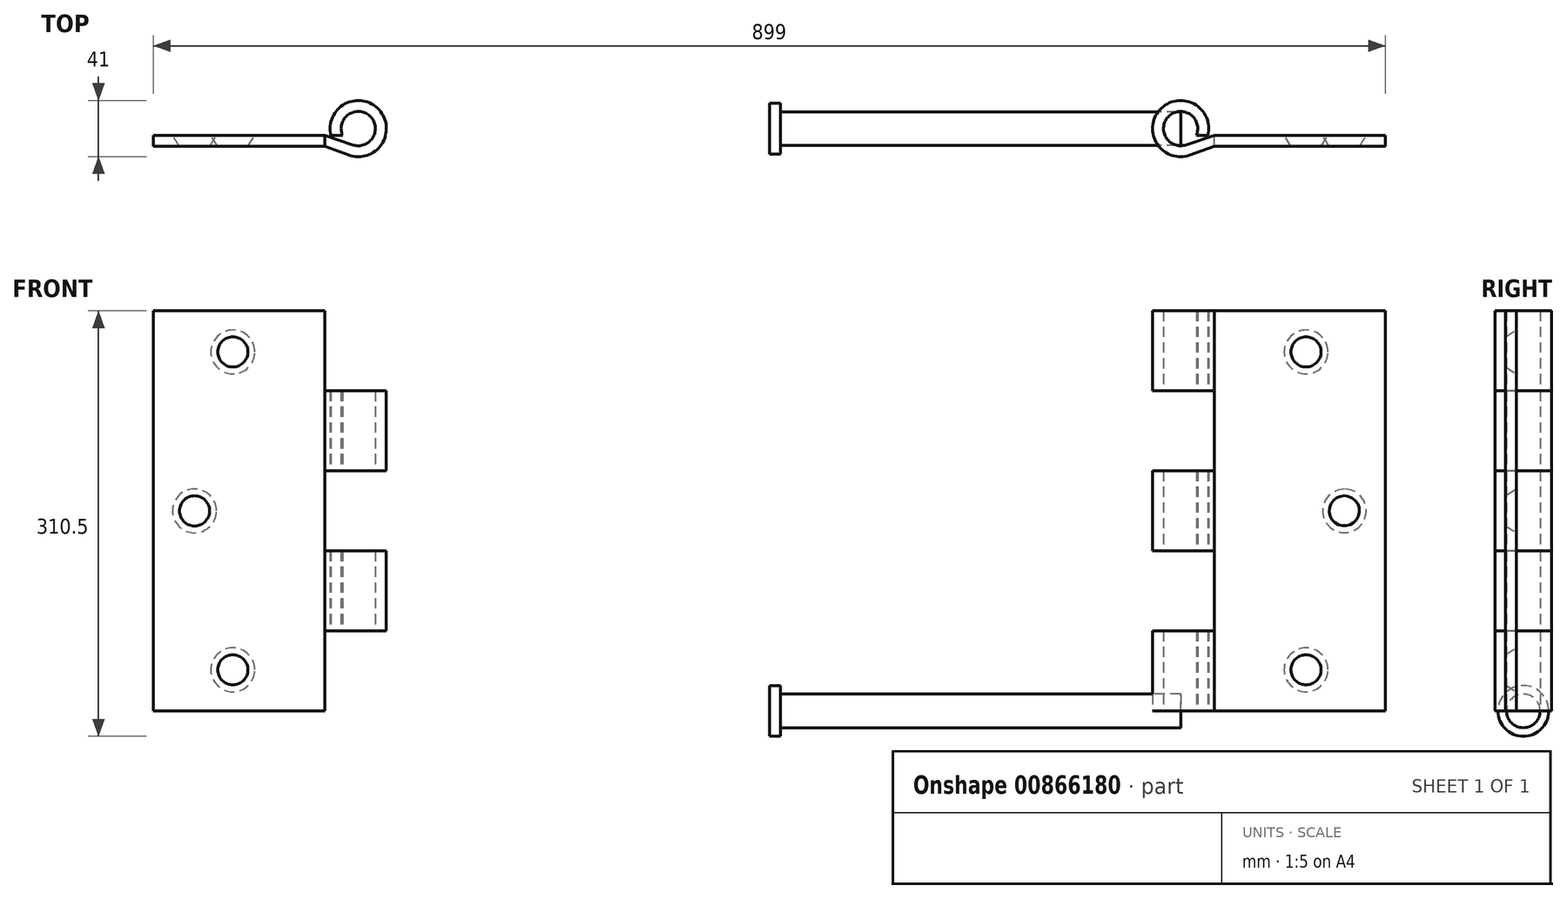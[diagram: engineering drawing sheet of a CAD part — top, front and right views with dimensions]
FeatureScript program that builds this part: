
annotation { "Feature Type Name" : "Feature", "Feature Type Description" : "" }
export const myFeature = defineFeature(function(context is Context, id is Id, definition is map)
    precondition{}
    {
        {
            var Q0;
            Q0=qCreatedBy(makeId("Top.planeOp"),FACE);
            var sketch = newSketch(context, id + "F0", { "sketchPlane" : qUnion([Q0])});
            skArc(sketch, "E0", {"start": v(-6.91, -19.3) * mm, "mid": v(15.19, 13.77) * mm, "end": v(-19.88, -5) * mm});
            skArc(sketch, "E1", {"start": v(-3.96, -11.86) * mm, "mid": v(8.44, 9.22) * mm, "end": v(-11.46, -5) * mm});
            skLineSegment(sketch, "E2", {"start": v(-149.5, -5) * mm, "end": v(-149.5, -13) * mm});
            skLineSegment(sketch, "E3", {"start": v(-149.5, -13) * mm, "end": v(-24.5, -13) * mm});
            skLineSegment(sketch, "E4", {"start": v(-24.5, -5) * mm, "end": v(-3.96, -11.86) * mm});
            skLineSegment(sketch, "E5", {"start": v(-24.5, -13) * mm, "end": v(-6.91, -19.3) * mm});
            skLineSegment(sketch, "E6.trimOffspring", {"start": v(-24.5, -5) * mm, "end": v(-149.5, -5) * mm});
            skLineSegment(sketch, "E7", {"start": v(-19.88, -5) * mm, "end": v(-11.46, -5) * mm});
            skSolve(sketch);
        }
        {
            var Q0;
            Q0=makeQuery(id+"F0.imprint","IMPRINT",FACE,{"disambiguationData":[TD([[makeQuery(id+"F0.imprint","IMPRINT",EDGE,{"derivedFrom":sQuery(id+"F0.wireOp",EDGE,"E0")}),1.0]])]});
            extrude(context, id + "F1", {"entities" : qUnion([Q0]), "depth" : 292 * mm, "offsetDistance" : 25 * mm});
        }
        {
            var Q0;
            Q0=makeQuery(id+"F1.opExtrude","SWEPT_FACE",FACE,{"disambiguationData":[OSD([sQuery(id+"F0.wireOp",EDGE,"E6.trimOffspring")])]});
            var sketch = newSketch(context, id + "F2", { "sketchPlane" : qUnion([Q0])});
            skCircle(sketch, "E8", {"center": v(119.5, 146) * mm, "radius": 16 * mm});
            skLineSegment(sketch, "E9", {"start": v(149.5, 30) * mm, "end": v(91.5, 30) * mm});
            skCircle(sketch, "E10", {"center": v(91.5, 30) * mm, "radius": 16 * mm});
            skCircle(sketch, "E11", {"center": v(91.5, 262) * mm, "radius": 16 * mm});
            skSolve(sketch);
        }
        {
            var Q0;
            Q0=makeQuery(id+"F1.opExtrude","SWEPT_FACE",FACE,{"disambiguationData":[OSD([sQuery(id+"F0.wireOp",EDGE,"E3")])]});
            var sketch = newSketch(context, id + "F3", { "sketchPlane" : qUnion([Q0])});
            skCircle(sketch, "E12", {"center": v(-91.5, 30) * mm, "radius": 11 * mm});
            skCircle(sketch, "E13", {"center": v(-119.43, 146) * mm, "radius": 11 * mm});
            skCircle(sketch, "E14", {"center": v(-91.5, 262) * mm, "radius": 11 * mm});
            skSolve(sketch);
        }
        {
            var Q1;
            Q1=makeQuery(id+"F2.imprint","IMPRINT",FACE,{"disambiguationData":[TD([[makeQuery(id+"F2.imprint","IMPRINT",EDGE,{"derivedFrom":sQuery(id+"F2.wireOp",EDGE,"E11")}),1.0]])]});
            var Q2;
            Q2=makeQuery(id+"F3.imprint","IMPRINT",FACE,{"disambiguationData":[TD([[makeQuery(id+"F3.imprint","IMPRINT",EDGE,{"derivedFrom":sQuery(id+"F3.wireOp",EDGE,"E14")}),1.0]])]});
            loft(context, id + "F4", {"operationType" : NewBodyOperationType.REMOVE, "sheetProfilesArray" : [{ "sheetProfileEntities" : qUnion([Q1]) }, { "sheetProfileEntities" : qUnion([Q2]) }]});
        }
        {
            var Q1;
            Q1=makeQuery(id+"F2.imprint","IMPRINT",FACE,{"disambiguationData":[TD([[makeQuery(id+"F2.imprint","IMPRINT",EDGE,{"derivedFrom":sQuery(id+"F2.wireOp",EDGE,"E8")}),1.0]])]});
            var Q2;
            Q2=makeQuery(id+"F3.imprint","IMPRINT",FACE,{"disambiguationData":[TD([[makeQuery(id+"F3.imprint","IMPRINT",EDGE,{"derivedFrom":sQuery(id+"F3.wireOp",EDGE,"E13")}),1.0]])]});
            loft(context, id + "F5", {"operationType" : NewBodyOperationType.REMOVE, "sheetProfilesArray" : [{ "sheetProfileEntities" : qUnion([Q1]) }, { "sheetProfileEntities" : qUnion([Q2]) }]});
        }
        {
            var Q1;
            Q1=makeQuery(id+"F2.imprint","IMPRINT",FACE,{"disambiguationData":[TD([[makeQuery(id+"F2.imprint","IMPRINT",EDGE,{"derivedFrom":sQuery(id+"F2.wireOp",EDGE,"E10")}),1.0]])]});
            var Q2;
            Q2=makeQuery(id+"F3.imprint","IMPRINT",FACE,{"disambiguationData":[TD([[makeQuery(id+"F3.imprint","IMPRINT",EDGE,{"derivedFrom":sQuery(id+"F3.wireOp",EDGE,"E12")}),1.0]])]});
            loft(context, id + "F6", {"operationType" : NewBodyOperationType.REMOVE, "sheetProfilesArray" : [{ "sheetProfileEntities" : qUnion([Q1]) }, { "sheetProfileEntities" : qUnion([Q2]) }]});
        }
        {
            var Q0;
            Q0=makeQuery(id+"F2.imprint","IMPRINT",FACE,{"disambiguationData":[TD([[makeQuery(id+"F2.imprint","IMPRINT",EDGE,{"derivedFrom":sQuery(id+"F2.wireOp",EDGE,"E8")}),-1.0]])]});
            var sketch = newSketch(context, id + "F7", { "sketchPlane" : qUnion([Q0])});
            skLineSegment(sketch, "E15.0", {"start": v(24.5, 292) * mm, "end": v(24.5, 0) * mm});
            skPoint(sketch, "E16.0", {"position": v(24.5, 292) * mm});
            skLineSegment(sketch, "E17.bottom", {"start": v(24.5, 292) * mm, "end": v(-25.5, 292) * mm});
            skLineSegment(sketch, "E17.top", {"start": v(24.5, 233.6) * mm, "end": v(-25.5, 233.6) * mm});
            skLineSegment(sketch, "E17.left", {"start": v(24.5, 292) * mm, "end": v(24.5, 233.6) * mm});
            skLineSegment(sketch, "E17.right", {"start": v(-25.5, 292) * mm, "end": v(-25.5, 233.6) * mm});
            skLineSegment(sketch, "E18.top", {"start": v(24.5, 175.2) * mm, "end": v(-25.5, 175.2) * mm});
            skLineSegment(sketch, "E18.left", {"start": v(24.5, 233.6) * mm, "end": v(24.5, 175.2) * mm});
            skLineSegment(sketch, "E18.right", {"start": v(-25.5, 233.6) * mm, "end": v(-25.5, 175.2) * mm});
            skLineSegment(sketch, "E19.top", {"start": v(24.5, 116.8) * mm, "end": v(-25.5, 116.8) * mm});
            skLineSegment(sketch, "E19.left", {"start": v(24.5, 175.2) * mm, "end": v(24.5, 116.8) * mm});
            skLineSegment(sketch, "E19.right", {"start": v(-25.5, 175.2) * mm, "end": v(-25.5, 116.8) * mm});
            skLineSegment(sketch, "E20.top", {"start": v(24.5, 58.4) * mm, "end": v(-25.5, 58.4) * mm});
            skLineSegment(sketch, "E20.left", {"start": v(24.5, 116.8) * mm, "end": v(24.5, 58.4) * mm});
            skLineSegment(sketch, "E20.right", {"start": v(-25.5, 116.8) * mm, "end": v(-25.5, 58.4) * mm});
            skLineSegment(sketch, "E21.top", {"start": v(24.5, 0) * mm, "end": v(-25.5, 0) * mm});
            skLineSegment(sketch, "E21.left", {"start": v(24.5, 58.4) * mm, "end": v(24.5, 0) * mm});
            skLineSegment(sketch, "E21.right", {"start": v(-25.5, 58.4) * mm, "end": v(-25.5, 0) * mm});
            skSolve(sketch);
        }
        {
            var Q0;
            Q0=qCreatedBy(makeId("Right.planeOp"),FACE);
            cPlane(context, id + "F8", {"entities" : qUnion([Q0]), "cplaneType" : CPlaneType.OFFSET, "offset" : 300 * mm, "width" : 150 * mm, "height" : 150 * mm});
        }
        {
            var Q0;
            Q0=makeQuery(id+"F1.opExtrude","SWEPT_BODY",BODY,{"disambiguationData":[OSD([sQuery(id+"F0.wireOp",EDGE,"E0"),sQuery(id+"F0.wireOp",EDGE,"E1"),sQuery(id+"F0.wireOp",EDGE,"E2"),sQuery(id+"F0.wireOp",EDGE,"E3"),sQuery(id+"F0.wireOp",EDGE,"E4"),sQuery(id+"F0.wireOp",EDGE,"E5"),sQuery(id+"F0.wireOp",EDGE,"E6.trimOffspring"),sQuery(id+"F0.wireOp",EDGE,"E7")])]});
            var Q1;
            Q1=qCreatedBy(id+"F8.planeOp",FACE);
            mirror(context, id + "F9", {"entities" : qUnion([Q0]), "mirrorPlane" : qUnion([Q1])});
        }
        {
            var Q0;
            Q0=makeQuery(id+"F9.opPattern","COPY",FACE,{"derivedFrom":makeQuery(id+"F1.opExtrude","SWEPT_FACE",FACE,{"disambiguationData":[OSD([sQuery(id+"F0.wireOp",EDGE,"E6.trimOffspring")])]}),"instanceName":"1"});
            var sketch = newSketch(context, id + "F10", { "sketchPlane" : qUnion([Q0])});
            skLineSegment(sketch, "E22.bottom", {"start": v(-624.5, 0) * mm, "end": v(-574.5, 0) * mm});
            skLineSegment(sketch, "E22.top", {"start": v(-624.5, 58.4) * mm, "end": v(-574.5, 58.4) * mm});
            skLineSegment(sketch, "E22.left", {"start": v(-624.5, 0) * mm, "end": v(-624.5, 58.4) * mm});
            skLineSegment(sketch, "E22.right", {"start": v(-574.5, 0) * mm, "end": v(-574.5, 58.4) * mm});
            skLineSegment(sketch, "E23.top", {"start": v(-624.5, 116.8) * mm, "end": v(-574.5, 116.8) * mm});
            skLineSegment(sketch, "E23.left", {"start": v(-624.5, 58.4) * mm, "end": v(-624.5, 116.8) * mm});
            skLineSegment(sketch, "E23.right", {"start": v(-574.5, 58.4) * mm, "end": v(-574.5, 116.8) * mm});
            skLineSegment(sketch, "E24.top", {"start": v(-624.5, 175.2) * mm, "end": v(-574.5, 175.2) * mm});
            skLineSegment(sketch, "E24.left", {"start": v(-624.5, 116.8) * mm, "end": v(-624.5, 175.2) * mm});
            skLineSegment(sketch, "E24.right", {"start": v(-574.5, 116.8) * mm, "end": v(-574.5, 175.2) * mm});
            skLineSegment(sketch, "E25.top", {"start": v(-624.5, 233.6) * mm, "end": v(-574.5, 233.6) * mm});
            skLineSegment(sketch, "E25.left", {"start": v(-624.5, 175.2) * mm, "end": v(-624.5, 233.6) * mm});
            skLineSegment(sketch, "E25.right", {"start": v(-574.5, 175.2) * mm, "end": v(-574.5, 233.6) * mm});
            skLineSegment(sketch, "E26.top", {"start": v(-624.5, 292) * mm, "end": v(-574.5, 292) * mm});
            skLineSegment(sketch, "E26.left", {"start": v(-624.5, 233.6) * mm, "end": v(-624.5, 292) * mm});
            skLineSegment(sketch, "E26.right", {"start": v(-574.5, 233.6) * mm, "end": v(-574.5, 292) * mm});
            skSolve(sketch);
        }
        {
            var Q0;
            Q0=makeQuery(id+"F10.imprint","IMPRINT",FACE,{"disambiguationData":[TD([[makeQuery(id+"F10.imprint","IMPRINT",EDGE,{"derivedFrom":sQuery(id+"F10.wireOp",EDGE,"E24.top")}),1.0]])]});
            var Q1;
            Q1=makeQuery(id+"F10.imprint","IMPRINT",FACE,{"disambiguationData":[TD([[makeQuery(id+"F10.imprint","IMPRINT",EDGE,{"derivedFrom":sQuery(id+"F10.wireOp",EDGE,"E22.top")}),1.0]])]});
            extrude(context, id + "F11", {"entities" : qUnion([Q0, Q1]), "operationType" : NewBodyOperationType.REMOVE, "endBound" : BoundingType.SYMMETRIC, "oppositeDirection" : true, "depth" : 100 * mm, "offsetDistance" : 25 * mm});
        }
        {
            var Q0;
            Q0=makeQuery(id+"F7.imprint","IMPRINT",FACE,{"disambiguationData":[TD([[makeQuery(id+"F7.imprint","IMPRINT",EDGE,{"derivedFrom":sQuery(id+"F7.wireOp",EDGE,"E20.top")}),1.0]])]});
            var Q1;
            Q1=makeQuery(id+"F7.imprint","IMPRINT",FACE,{"disambiguationData":[TD([[makeQuery(id+"F7.imprint","IMPRINT",EDGE,{"derivedFrom":sQuery(id+"F7.wireOp",EDGE,"E18.top")}),1.0]])]});
            var Q2;
            Q2=makeQuery(id+"F7.imprint","IMPRINT",FACE,{"disambiguationData":[TD([[makeQuery(id+"F7.imprint","IMPRINT",EDGE,{"derivedFrom":sQuery(id+"F7.wireOp",EDGE,"E17.bottom")}),1.0]])]});
            extrude(context, id + "F12", {"entities" : qUnion([Q0, Q1, Q2]), "operationType" : NewBodyOperationType.REMOVE, "endBound" : BoundingType.SYMMETRIC, "depth" : 100 * mm, "offsetDistance" : 25 * mm});
        }
        {
            var Q0;
            Q0=qCreatedBy(id+"F8.planeOp",FACE);
            var sketch = newSketch(context, id + "F13", { "sketchPlane" : qUnion([Q0])});
            skCircle(sketch, "E27", {"center": v(0, 0) * mm, "radius": 12.25 * mm});
            skCircle(sketch, "E28", {"center": v(0, 0) * mm, "radius": 18.5 * mm});
            skSolve(sketch);
        }
        {
            var Q0;
            Q0=makeQuery(id+"F13.imprint","IMPRINT",FACE,{"disambiguationData":[TD([[makeQuery(id+"F13.imprint","IMPRINT",EDGE,{"derivedFrom":sQuery(id+"F13.wireOp",EDGE,"E27")}),1.0]])]});
            extrude(context, id + "F14", {"entities" : qUnion([Q0]), "depth" : 300 * mm, "offsetDistance" : 25 * mm});
        }
        {
            var Q0;
            Q0=makeQuery(id+"F13.imprint","IMPRINT",FACE,{"disambiguationData":[TD([[makeQuery(id+"F13.imprint","IMPRINT",EDGE,{"derivedFrom":sQuery(id+"F13.wireOp",EDGE,"E27")}),-1.0]])]});
            extrude(context, id + "F15", {"entities" : qUnion([Q0]), "operationType" : NewBodyOperationType.ADD, "depth" : 8 * mm, "offsetDistance" : 25 * mm});
        }
    });
